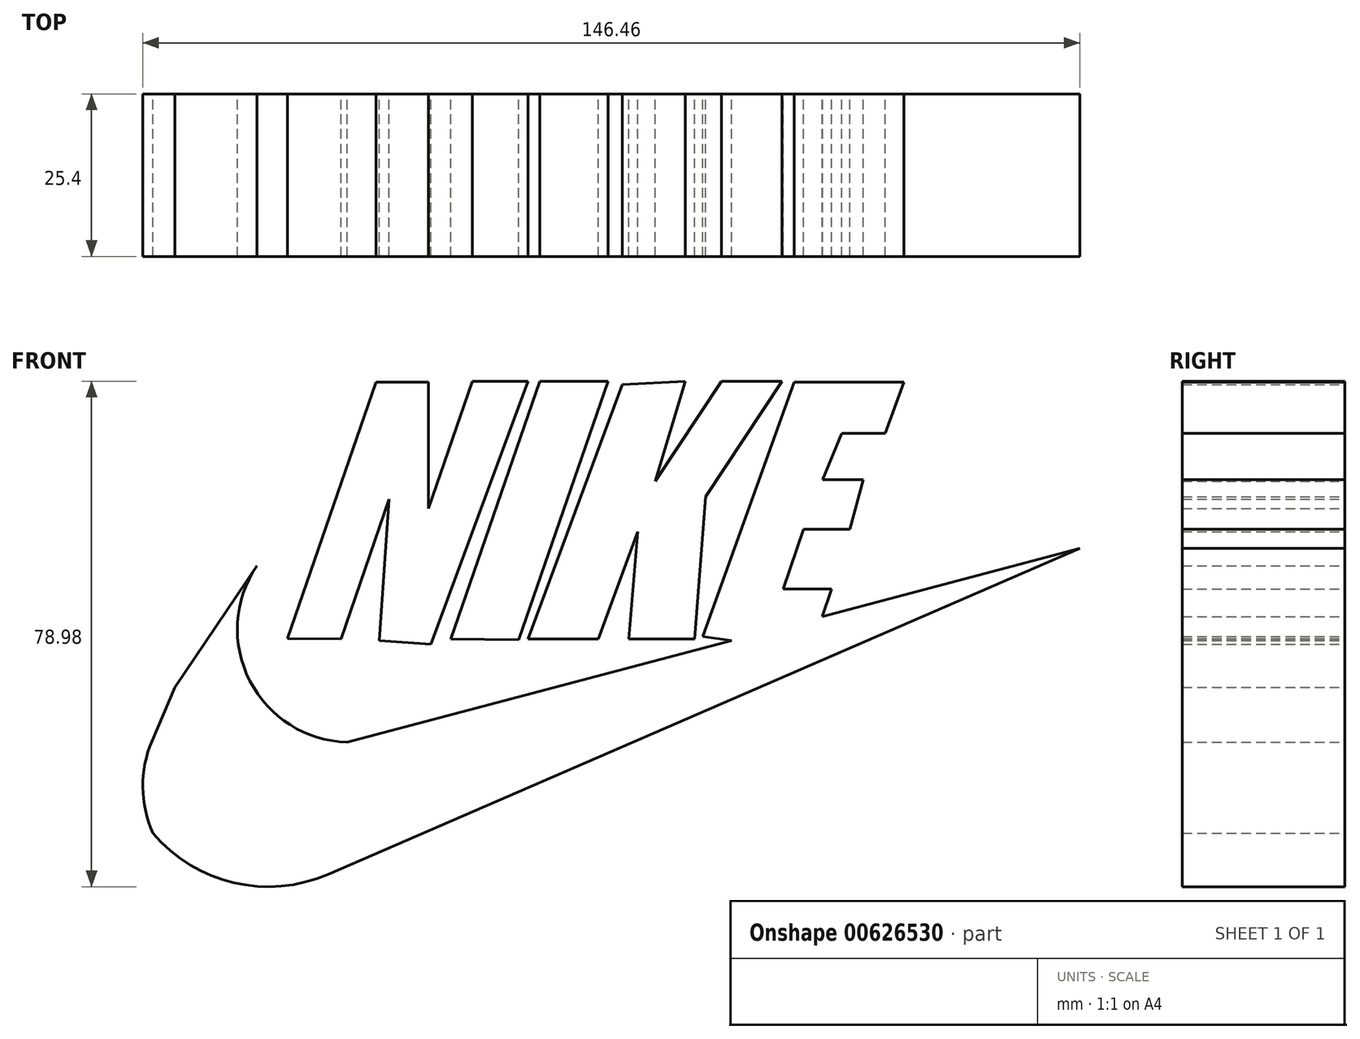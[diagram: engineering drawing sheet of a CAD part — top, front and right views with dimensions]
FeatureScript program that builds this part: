
annotation { "Feature Type Name" : "Feature", "Feature Type Description" : "" }
export const myFeature = defineFeature(function(context is Context, id is Id, definition is map)
    precondition{}
    {
        {
            var Q0;
            Q0=qCreatedBy(makeId("Front.planeOp"),FACE);
            var sketch = newSketch(context, id + "F0", { "sketchPlane" : qUnion([Q0])});
            skLineSegment(sketch, "E0", {"start": v(77.05, 38.99) * mm, "end": v(-40.4, -11.91) * mm});
            skArc(sketch, "E1", {"start": v(-67.84, -5.48) * mm, "mid": v(-55.18, -13.24) * mm, "end": v(-40.4, -11.91) * mm});
            skLineSegment(sketch, "E2", {"start": v(-64.42, 17.31) * mm, "end": v(-51.6, 36.26) * mm});
            skLineSegment(sketch, "E3", {"start": v(-64.42, 17.31) * mm, "end": v(-67.98, 8.9) * mm});
            skArc(sketch, "E4", {"start": v(-67.98, 8.9) * mm, "mid": v(-69.4, 1.7) * mm, "end": v(-67.84, -5.48) * mm});
            skLineSegment(sketch, "E5", {"start": v(-37.47, 8.72) * mm, "end": v(77.05, 38.99) * mm});
            skArc(sketch, "E6", {"start": v(-51.6, 36.26) * mm, "mid": v(-52.68, 18.31) * mm, "end": v(-37.47, 8.72) * mm});
            skLineSegment(sketch, "E7", {"start": v(-38.45, 24.83) * mm, "end": v(-30.9, 46.67) * mm});
            skLineSegment(sketch, "E8", {"start": v(-30.9, 46.67) * mm, "end": v(-32.47, 24.57) * mm});
            skLineSegment(sketch, "E9", {"start": v(-32.47, 24.57) * mm, "end": v(-24.4, 24) * mm});
            skLineSegment(sketch, "E10", {"start": v(-24.4, 24) * mm, "end": v(-9.2, 65.12) * mm});
            skLineSegment(sketch, "E11", {"start": v(-9.2, 65.12) * mm, "end": v(-17.91, 65.12) * mm});
            skLineSegment(sketch, "E12", {"start": v(-17.91, 65.12) * mm, "end": v(-24.78, 45.23) * mm});
            skLineSegment(sketch, "E13", {"start": v(-24.78, 45.23) * mm, "end": v(-24.78, 64.99) * mm});
            skLineSegment(sketch, "E14", {"start": v(-24.78, 64.99) * mm, "end": v(-32.99, 64.99) * mm});
            skLineSegment(sketch, "E15", {"start": v(-32.99, 64.99) * mm, "end": v(-46.82, 24.93) * mm});
            skLineSegment(sketch, "E16", {"start": v(-46.82, 24.93) * mm, "end": v(-38.45, 24.83) * mm});
            skLineSegment(sketch, "E17", {"start": v(-21.3, 24.83) * mm, "end": v(-7.39, 65.12) * mm});
            skLineSegment(sketch, "E18", {"start": v(-7.39, 65.12) * mm, "end": v(3.27, 65.12) * mm});
            skLineSegment(sketch, "E19", {"start": v(3.27, 65.12) * mm, "end": v(-10.68, 24.72) * mm});
            skLineSegment(sketch, "E20", {"start": v(-10.68, 24.72) * mm, "end": v(-21.3, 24.83) * mm});
            skLineSegment(sketch, "E21", {"start": v(-9.2, 24.83) * mm, "end": v(5.5, 64.6) * mm});
            skLineSegment(sketch, "E22", {"start": v(5.5, 64.6) * mm, "end": v(15.38, 65.12) * mm});
            skLineSegment(sketch, "E23", {"start": v(15.38, 65.12) * mm, "end": v(10.67, 49.5) * mm});
            skLineSegment(sketch, "E24", {"start": v(10.67, 49.5) * mm, "end": v(21, 65.12) * mm});
            skLineSegment(sketch, "E25", {"start": v(21, 65.12) * mm, "end": v(30.5, 65.12) * mm});
            skLineSegment(sketch, "E26", {"start": v(30.5, 65.12) * mm, "end": v(18.55, 47.04) * mm});
            skLineSegment(sketch, "E27", {"start": v(18.55, 47.04) * mm, "end": v(16.83, 24.83) * mm});
            skLineSegment(sketch, "E28", {"start": v(16.83, 24.83) * mm, "end": v(6.5, 24.83) * mm});
            skLineSegment(sketch, "E29", {"start": v(6.5, 24.83) * mm, "end": v(7.95, 41.61) * mm});
            skLineSegment(sketch, "E30", {"start": v(7.95, 41.61) * mm, "end": v(1.75, 24.83) * mm});
            skLineSegment(sketch, "E31", {"start": v(1.75, 24.83) * mm, "end": v(-9.2, 24.83) * mm});
            skLineSegment(sketch, "E32", {"start": v(18.1, 25.22) * mm, "end": v(32.4, 64.98) * mm});
            skLineSegment(sketch, "E33", {"start": v(32.4, 64.98) * mm, "end": v(49.52, 64.98) * mm});
            skLineSegment(sketch, "E34", {"start": v(49.52, 64.98) * mm, "end": v(46.63, 57) * mm});
            skLineSegment(sketch, "E35", {"start": v(46.63, 57) * mm, "end": v(39.83, 57) * mm});
            skLineSegment(sketch, "E36", {"start": v(39.83, 57) * mm, "end": v(36.84, 49.76) * mm});
            skLineSegment(sketch, "E37", {"start": v(36.84, 49.76) * mm, "end": v(43.18, 49.76) * mm});
            skLineSegment(sketch, "E38", {"start": v(43.18, 49.76) * mm, "end": v(41.1, 41.97) * mm});
            skLineSegment(sketch, "E39", {"start": v(41.1, 41.97) * mm, "end": v(33.85, 41.97) * mm});
            skLineSegment(sketch, "E40", {"start": v(33.85, 41.97) * mm, "end": v(30.68, 32.64) * mm});
            skLineSegment(sketch, "E41", {"start": v(30.68, 32.64) * mm, "end": v(38.23, 32.64) * mm});
            skLineSegment(sketch, "E42", {"start": v(38.23, 32.64) * mm, "end": v(36.47, 27.47) * mm});
            skLineSegment(sketch, "E43", {"start": v(18.1, 25.22) * mm, "end": v(22.58, 24.6) * mm});
            skSolve(sketch);
        }
        {
            var Q0;
            Q0=makeQuery(id+"F0.imprint","IMPRINT",FACE,{"disambiguationData":[TD([[makeQuery(id+"F0.imprint","IMPRINT",EDGE,{"derivedFrom":sQuery(id+"F0.wireOp",EDGE,"E7")}),1.0]])]});
            var Q1;
            Q1=makeQuery(id+"F0.imprint","IMPRINT",FACE,{"disambiguationData":[TD([[makeQuery(id+"F0.imprint","IMPRINT",EDGE,{"derivedFrom":sQuery(id+"F0.wireOp",EDGE,"E17")}),-1.0]])]});
            var Q2;
            Q2=makeQuery(id+"F0.imprint","IMPRINT",FACE,{"disambiguationData":[TD([[makeQuery(id+"F0.imprint","IMPRINT",EDGE,{"derivedFrom":sQuery(id+"F0.wireOp",EDGE,"E21")}),-1.0]])]});
            var Q3;
            Q3=makeQuery(id+"F0.imprint","IMPRINT",FACE,{"disambiguationData":[TD([[makeQuery(id+"F0.imprint","IMPRINT",EDGE,{"derivedFrom":sQuery(id+"F0.wireOp",EDGE,"E32")}),-1.0]])]});
            var Q4;
            {var subQ0=sQuery(id+"F0.wireOp",EDGE,"E0");Q4=makeQuery(id+"F0.imprint","IMPRINT",FACE,{"disambiguationData":[TD([[makeQuery(id+"F0.imprint","IMPRINT",EDGE,{"derivedFrom":subQ0}),-1.0]])]});}
            extrude(context, id + "F1", {"entities" : qUnion([Q0, Q1, Q2, Q3, Q4]), "depth" : 25.4 * mm, "offsetDistance" : 25.4 * mm});
        }
    });
